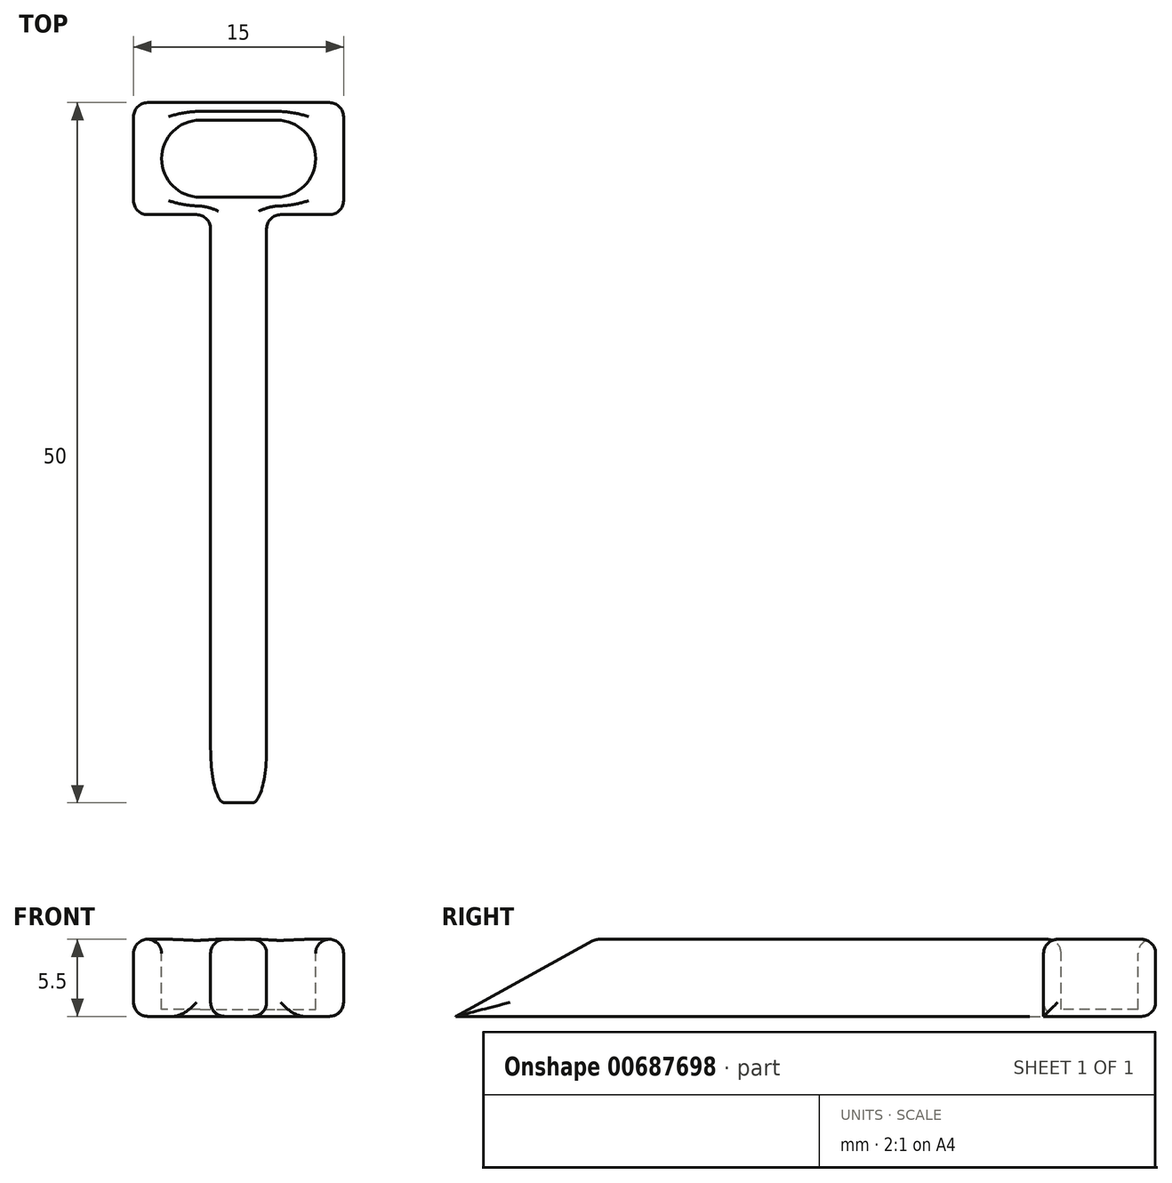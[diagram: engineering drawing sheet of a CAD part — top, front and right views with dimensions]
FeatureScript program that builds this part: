
annotation { "Feature Type Name" : "Feature", "Feature Type Description" : "" }
export const myFeature = defineFeature(function(context is Context, id is Id, definition is map)
    precondition{}
    {
        {
            var Q0;
            Q0=qCreatedBy(makeId("Right.planeOp"),FACE);
            var sketch = newSketch(context, id + "F0", { "sketchPlane" : qUnion([Q0])});
            skLineSegment(sketch, "E0", {"start": v(10, 5.5) * mm, "end": v(42, 5.5) * mm});
            skLineSegment(sketch, "E1", {"start": v(42, 5.5) * mm, "end": v(42, 0) * mm});
            skLineSegment(sketch, "E2", {"start": v(42, 0) * mm, "end": v(0, 0) * mm});
            skLineSegment(sketch, "E3", {"start": v(0, 0) * mm, "end": v(10, 5.5) * mm});
            skLineSegment(sketch, "E4", {"start": v(42, 5.5) * mm, "end": v(50, 5.5) * mm});
            skLineSegment(sketch, "E5", {"start": v(50, 5.5) * mm, "end": v(50, 0) * mm});
            skLineSegment(sketch, "E6", {"start": v(50, 0) * mm, "end": v(42, 0) * mm});
            skSolve(sketch);
        }
        {
            var Q0;
            Q0=makeQuery(id+"F0.imprint","IMPRINT",FACE,{"disambiguationData":[TD([[makeQuery(id+"F0.imprint","IMPRINT",EDGE,{"derivedFrom":sQuery(id+"F0.wireOp",EDGE,"E0")}),-1.0]])]});
            extrude(context, id + "F1", {"entities" : qUnion([Q0]), "depth" : 4 * mm, "offsetDistance" : 25 * mm, "symmetric" : true});
        }
        {
            var Q0;
            Q0=makeQuery(id+"F0.imprint","IMPRINT",FACE,{"disambiguationData":[TD([[makeQuery(id+"F0.imprint","IMPRINT",EDGE,{"derivedFrom":sQuery(id+"F0.wireOp",EDGE,"E1")}),1.0]])]});
            extrude(context, id + "F2", {"entities" : qUnion([Q0]), "operationType" : NewBodyOperationType.ADD, "depth" : 15 * mm, "offsetDistance" : 25 * mm, "symmetric" : true});
        }
        {
            var Q0;
            Q0=makeQuery(id+"F2.boolean.opBoolean","MERGE",FACE,{"derivedFrom":[makeQuery(id+"F1.opExtrude","SWEPT_FACE",FACE,{"disambiguationData":[OSD([sQuery(id+"F0.wireOp",EDGE,"E0")])]}),makeQuery(id+"F2.opExtrude","SWEPT_FACE",FACE,{"disambiguationData":[OSD([sQuery(id+"F0.wireOp",EDGE,"E4")])]})]});
            var sketch = newSketch(context, id + "F3", { "sketchPlane" : qUnion([Q0])});
            skLineSegment(sketch, "E7", {"start": v(0, 63.49) * mm, "end": v(0, -7.44) * mm, "construction": true});
            skLineSegment(sketch, "E8", {"start": v(14.98, 46) * mm, "end": v(-20.48, 46) * mm, "construction": true});
            skPoint(sketch, "E8.startSnap0", {"position": v(7.5, 46) * mm});
            skLineSegment(sketch, "E9.bottom", {"start": v(-2.75, 48.75) * mm, "end": v(2.75, 48.75) * mm, "construction": true});
            skLineSegment(sketch, "E9.top", {"start": v(-2.75, 43.25) * mm, "end": v(2.75, 43.25) * mm, "construction": true});
            skLineSegment(sketch, "E9.left", {"start": v(-2.75, 48.75) * mm, "end": v(-2.75, 43.25) * mm, "construction": true});
            skLineSegment(sketch, "E9.right", {"start": v(2.75, 48.75) * mm, "end": v(2.75, 43.25) * mm, "construction": true});
            skPoint(sketch, "E9.middle", {"position": v(0, 46) * mm});
            skArc(sketch, "E10", {"start": v(-2.75, 43.25) * mm, "mid": v(-5.5, 46) * mm, "end": v(-2.75, 48.75) * mm});
            skArc(sketch, "E11", {"start": v(2.75, 43.25) * mm, "mid": v(5.5, 46) * mm, "end": v(2.75, 48.75) * mm});
            skLineSegment(sketch, "E12", {"start": v(-2.75, 48.75) * mm, "end": v(2.75, 48.75) * mm});
            skLineSegment(sketch, "E13", {"start": v(2.75, 43.25) * mm, "end": v(-2.75, 43.25) * mm});
            skSolve(sketch);
        }
        {
            var Q0;
            Q0 = qSketchRegion(id + "F3", true);
            extrude(context, id + "F4", {"entities" : qUnion([Q0]), "operationType" : NewBodyOperationType.REMOVE, "oppositeDirection" : true, "depth" : 5 * mm, "offsetDistance" : 25 * mm});
        }
        {
            var Q0;
            Q0=makeQuery(id+"F3.imprint","IMPRINT",FACE,{"disambiguationData":[TD([[makeQuery(id+"F3.imprint","IMPRINT",EDGE,{"derivedFrom":sQuery(id+"F3.wireOp",EDGE,"E10")}),-1.0]])]});
            extrude(context, id + "F5", {"entities" : qUnion([Q0]), "operationType" : NewBodyOperationType.ADD, "oppositeDirection" : true, "depth" : 0.5 * mm, "offsetDistance" : 25 * mm});
        }
        {
            var Q0;
            Q0=makeQuery(id+"F2.opExtrude","CAP_EDGE",EDGE,{"disambiguationData":[OSD([sQuery(id+"F0.wireOp",EDGE,"E1")])],"isStart":true});
            var Q1;
            Q1=makeQuery(id+"F2.opExtrude","CAP_EDGE",EDGE,{"disambiguationData":[OSD([sQuery(id+"F0.wireOp",EDGE,"E5")])],"isStart":true});
            var Q2;
            Q2=makeQuery(id+"F2.opExtrude","CAP_EDGE",EDGE,{"disambiguationData":[OSD([sQuery(id+"F0.wireOp",EDGE,"E5")])],"isStart":false});
            var Q3;
            Q3=makeQuery(id+"F2.opExtrude","CAP_EDGE",EDGE,{"disambiguationData":[OSD([sQuery(id+"F0.wireOp",EDGE,"E1")])],"isStart":false});
            var Q4;
            Q4=makeQuery(id+"F1.opExtrude","CAP_EDGE",EDGE,{"disambiguationData":[OSD([sQuery(id+"F0.wireOp",EDGE,"E1")])],"isStart":false});
            var Q5;
            Q5=makeQuery(id+"F1.opExtrude","CAP_EDGE",EDGE,{"disambiguationData":[OSD([sQuery(id+"F0.wireOp",EDGE,"E1")])],"isStart":true});
            var Q6;
            Q6=makeQuery(id+"F5.boolean.opBoolean","MERGE",FACE,{"derivedFrom":[makeQuery(id+"F2.boolean.opBoolean","MERGE",FACE,{"derivedFrom":[makeQuery(id+"F1.opExtrude","SWEPT_FACE",FACE,{"disambiguationData":[OSD([sQuery(id+"F0.wireOp",EDGE,"E0")])]}),makeQuery(id+"F2.opExtrude","SWEPT_FACE",FACE,{"disambiguationData":[OSD([sQuery(id+"F0.wireOp",EDGE,"E4")])]})]}),makeQuery(id+"F5.opExtrude","CAP_FACE",FACE,{"disambiguationData":[OSD([sQuery(id+"F3.wireOp",EDGE,"E10"),sQuery(id+"F3.wireOp",EDGE,"E11"),sQuery(id+"F3.wireOp",EDGE,"E12"),sQuery(id+"F3.wireOp",EDGE,"E13")])],"isStart":true})]});
            var Q7;
            Q7=makeQuery(id+"F1.opExtrude","CAP_FACE",FACE,{"disambiguationData":[OSD([sQuery(id+"F0.wireOp",EDGE,"E0"),sQuery(id+"F0.wireOp",EDGE,"E1"),sQuery(id+"F0.wireOp",EDGE,"E2"),sQuery(id+"F0.wireOp",EDGE,"E3")])],"isStart":false});
            var Q8;
            Q8=makeQuery(id+"F1.opExtrude","CAP_FACE",FACE,{"disambiguationData":[OSD([sQuery(id+"F0.wireOp",EDGE,"E0"),sQuery(id+"F0.wireOp",EDGE,"E1"),sQuery(id+"F0.wireOp",EDGE,"E2"),sQuery(id+"F0.wireOp",EDGE,"E3")])],"isStart":true});
            var Q9;
            Q9=makeQuery(id+"F2.opExtrude","SWEPT_FACE",FACE,{"disambiguationData":[OSD([sQuery(id+"F0.wireOp",EDGE,"E5")])]});
            var Q10;
            Q10=makeQuery(id+"F2.opExtrude","CAP_FACE",FACE,{"disambiguationData":[OSD([sQuery(id+"F0.wireOp",EDGE,"E1"),sQuery(id+"F0.wireOp",EDGE,"E4"),sQuery(id+"F0.wireOp",EDGE,"E5"),sQuery(id+"F0.wireOp",EDGE,"E6")])],"isStart":false});
            var Q11;
            Q11=makeQuery(id+"F2.opExtrude","CAP_FACE",FACE,{"disambiguationData":[OSD([sQuery(id+"F0.wireOp",EDGE,"E1"),sQuery(id+"F0.wireOp",EDGE,"E4"),sQuery(id+"F0.wireOp",EDGE,"E5"),sQuery(id+"F0.wireOp",EDGE,"E6")])],"isStart":true});
            fillet(context, id + "F6", {"entities" : qUnion([Q0, Q1, Q2, Q3, Q4, Q5, Q6, Q7, Q8, Q9, Q10, Q11]), "radius" : 1 * mm, "tangentPropagation" : true, "allowEdgeOverflow" : false});
        }
    });
